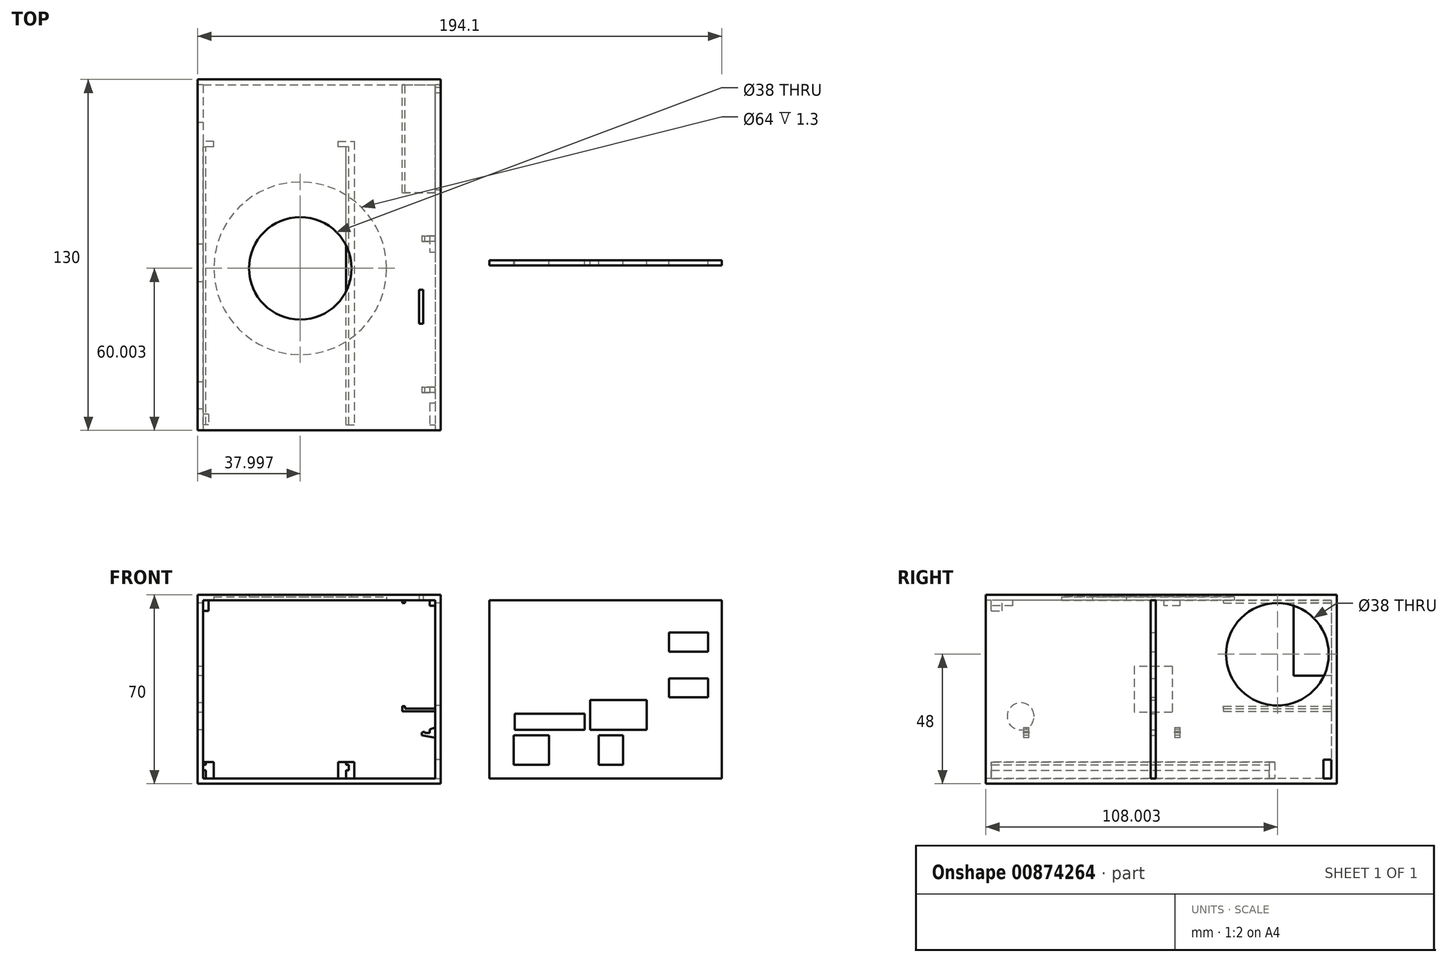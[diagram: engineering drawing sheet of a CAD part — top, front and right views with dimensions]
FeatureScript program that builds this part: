
annotation { "Feature Type Name" : "Feature", "Feature Type Description" : "" }
export const myFeature = defineFeature(function(context is Context, id is Id, definition is map)
    precondition{}
    {
        {
            var Q0;
            Q0=qCreatedBy(makeId("Top.planeOp"),FACE);
            var sketch = newSketch(context, id + "F0", { "sketchPlane" : qUnion([Q0])});
            skLineSegment(sketch, "E0.bottom", {"start": v(-34.75, 67) * mm, "end": v(55.25, 67) * mm});
            skLineSegment(sketch, "E0.top", {"start": v(-34.75, -63) * mm, "end": v(55.25, -63) * mm});
            skLineSegment(sketch, "E0.left", {"start": v(-34.75, 67) * mm, "end": v(-34.75, -63) * mm});
            skLineSegment(sketch, "E0.right", {"start": v(55.25, 67) * mm, "end": v(55.25, -63) * mm});
            skSolve(sketch);
        }
        {
            var Q0;
            Q0=makeQuery(id+"F0.imprint","IMPRINT",FACE,{"disambiguationData":[TD([[makeQuery(id+"F0.imprint","IMPRINT",EDGE,{"derivedFrom":sQuery(id+"F0.wireOp",EDGE,"E0.bottom")}),-1.0]])]});
            extrude(context, id + "F1", {"entities" : qUnion([Q0]), "depth" : 70 * mm, "offsetDistance" : 25 * mm});
        }
        {
            var Q0;
            Q0=makeQuery(id+"F1.opExtrude","SWEPT_FACE",FACE,{"disambiguationData":[OSD([sQuery(id+"F0.wireOp",EDGE,"E0.top")])]});
            var Q1;
            Q1=makeQuery(id+"F1.opExtrude","SWEPT_BODY",BODY,{"disambiguationData":[OSD([sQuery(id+"F0.wireOp",EDGE,"E0.bottom"),sQuery(id+"F0.wireOp",EDGE,"E0.top"),sQuery(id+"F0.wireOp",EDGE,"E0.left"),sQuery(id+"F0.wireOp",EDGE,"E0.right")])]});
            shell(context, id + "F2", {"entities" : qUnion([Q0]), "parts" : qUnion([Q1]), "thickness" : 2 * mm});
        }
        {
            var Q0;
            {var subQ0=sQuery(id+"F0.wireOp",EDGE,"E0.right");var subQ1=sQuery(id+"F0.wireOp",EDGE,"E0.left");var subQ2=sQuery(id+"F0.wireOp",EDGE,"E0.top");var subQ3=sQuery(id+"F0.wireOp",EDGE,"E0.bottom");Q0=makeQuery(id+"F2.opShell","OFFSET_FACE",FACE,{"disambiguationData":[OSD([subQ3,subQ2,subQ1,subQ0]),TDD([makeQuery(id+"F1.opExtrude","CAP_FACE",FACE,{"disambiguationData":[OSD([subQ3,subQ2,subQ1,subQ0])],"isStart":true})])]});}
            var sketch = newSketch(context, id + "F3", { "sketchPlane" : qUnion([Q0])});
            skLineSegment(sketch, "E1", {"start": v(-28.75, 42) * mm, "end": v(-28.75, 44) * mm});
            skLineSegment(sketch, "E2", {"start": v(17.25, 42) * mm, "end": v(17.25, 44) * mm});
            skLineSegment(sketch, "E3", {"start": v(17.25, 44) * mm, "end": v(23.25, 44) * mm});
            skLineSegment(sketch, "E4", {"start": v(23.25, 44) * mm, "end": v(23.25, 42) * mm});
            skLineSegment(sketch, "E5", {"start": v(-28.75, 44) * mm, "end": v(-32.75, 44) * mm});
            skLineSegment(sketch, "E6", {"start": v(-32.75, 44) * mm, "end": v(-32.75, 42) * mm});
            skLineSegment(sketch, "E7", {"start": v(23.25, 42) * mm, "end": v(17.25, 42) * mm});
            skLineSegment(sketch, "E8", {"start": v(-28.75, 42) * mm, "end": v(-32.75, 42) * mm});
            skSolve(sketch);
        }
        {
            var Q0;
            Q0=makeQuery(id+"F3.imprint","IMPRINT",FACE,{"disambiguationData":[TD([[makeQuery(id+"F3.imprint","IMPRINT",EDGE,{"derivedFrom":sQuery(id+"F3.wireOp",EDGE,"E1")}),1.0]])]});
            var Q1;
            Q1=makeQuery(id+"F3.imprint","IMPRINT",FACE,{"disambiguationData":[TD([[makeQuery(id+"F3.imprint","IMPRINT",EDGE,{"derivedFrom":sQuery(id+"F3.wireOp",EDGE,"E2")}),-1.0]])]});
            extrude(context, id + "F4", {"entities" : qUnion([Q0, Q1]), "operationType" : NewBodyOperationType.ADD, "depth" : 6 * mm, "offsetDistance" : 25 * mm});
        }
        {
            var Q0;
            Q0=makeQuery(id+"F4.opExtrude","SWEPT_FACE",FACE,{"disambiguationData":[OSD([sQuery(id+"F3.wireOp",EDGE,"E8")])]});
            var sketch = newSketch(context, id + "F5", { "sketchPlane" : qUnion([Q0])});
            skLineSegment(sketch, "E9", {"start": v(-32.75, 2) * mm, "end": v(-31.75, 2) * mm});
            skLineSegment(sketch, "E10", {"start": v(-31.75, 2) * mm, "end": v(-31.75, 5) * mm});
            skLineSegment(sketch, "E11", {"start": v(-31.75, 5) * mm, "end": v(-32.75, 5) * mm});
            skLineSegment(sketch, "E12", {"start": v(-32.75, 5) * mm, "end": v(-32.75, 2) * mm});
            skLineSegment(sketch, "E13", {"start": v(21.25, 7) * mm, "end": v(21.25, 5) * mm});
            skLineSegment(sketch, "E14", {"start": v(21.25, 5) * mm, "end": v(20.25, 5) * mm});
            skLineSegment(sketch, "E15", {"start": v(20.25, 5) * mm, "end": v(20.25, 2) * mm});
            skLineSegment(sketch, "E16", {"start": v(20.25, 2) * mm, "end": v(23.25, 2) * mm});
            skLineSegment(sketch, "E17", {"start": v(23.25, 2) * mm, "end": v(23.25, 8) * mm});
            skLineSegment(sketch, "E18", {"start": v(23.25, 8) * mm, "end": v(20.25, 8) * mm});
            skLineSegment(sketch, "E19", {"start": v(20.25, 8) * mm, "end": v(20.25, 7) * mm});
            skLineSegment(sketch, "E20", {"start": v(20.25, 7) * mm, "end": v(21.25, 7) * mm});
            skLineSegment(sketch, "E21.bottom", {"start": v(-32.75, 8) * mm, "end": v(-31.75, 8) * mm});
            skLineSegment(sketch, "E21.top", {"start": v(-32.75, 7) * mm, "end": v(-31.75, 7) * mm});
            skLineSegment(sketch, "E21.left", {"start": v(-32.75, 8) * mm, "end": v(-32.75, 7) * mm});
            skLineSegment(sketch, "E21.right", {"start": v(-31.75, 8) * mm, "end": v(-31.75, 7) * mm});
            skSolve(sketch);
        }
        {
            var Q0;
            Q0=makeQuery(id+"F5.imprint","IMPRINT",FACE,{"disambiguationData":[TD([[makeQuery(id+"F5.imprint","IMPRINT",EDGE,{"derivedFrom":sQuery(id+"F5.wireOp",EDGE,"E13")}),1.0]])]});
            var Q1;
            Q1=makeQuery(id+"F5.imprint","IMPRINT",FACE,{"disambiguationData":[TD([[makeQuery(id+"F5.imprint","IMPRINT",EDGE,{"derivedFrom":sQuery(id+"F5.wireOp",EDGE,"7ee66804-56aa-43c3-9890-e0b70faa4ac7")}),1.0]])]});
            var Q2;
            Q2=makeQuery(id+"F5.imprint","IMPRINT",FACE,{"disambiguationData":[TD([[makeQuery(id+"F5.imprint","IMPRINT",EDGE,{"derivedFrom":sQuery(id+"F5.wireOp",EDGE,"E9")}),-1.0]])]});
            var Q3;
            Q3=makeQuery(id+"F5.imprint","IMPRINT",FACE,{"disambiguationData":[TD([[makeQuery(id+"F5.imprint","IMPRINT",EDGE,{"derivedFrom":sQuery(id+"F5.wireOp",EDGE,"E21.bottom")}),1.0]])]});
            extrude(context, id + "F6", {"entities" : qUnion([Q0, Q1, Q2, Q3]), "operationType" : NewBodyOperationType.ADD, "depth" : 103 * mm, "offsetDistance" : 25 * mm});
        }
        {
            var Q0;
            Q0=makeQuery(id+"F2.opShell","OFFSET_FACE",FACE,{"disambiguationData":[OSD([sQuery(id+"F0.wireOp",EDGE,"E0.right")])]});
            var sketch = newSketch(context, id + "F7", { "sketchPlane" : qUnion([Q0])});
            skLineSegment(sketch, "E22", {"start": v(-9, 17.1) * mm, "end": v(-7, 17.1) * mm});
            skLineSegment(sketch, "E23", {"start": v(-7, 20.9) * mm, "end": v(-9, 20.9) * mm});
            skLineSegment(sketch, "E24", {"start": v(-9, 17.1) * mm, "end": v(-9, 20.9) * mm});
            skLineSegment(sketch, "E25", {"start": v(-7, 20.9) * mm, "end": v(-7, 17.1) * mm});
            skLineSegment(sketch, "E26", {"start": v(47, 17.1) * mm, "end": v(49, 17.1) * mm});
            skLineSegment(sketch, "E27", {"start": v(49, 20.9) * mm, "end": v(47, 20.9) * mm});
            skLineSegment(sketch, "E28", {"start": v(47, 17.1) * mm, "end": v(47, 20.9) * mm});
            skLineSegment(sketch, "E29", {"start": v(49, 20.9) * mm, "end": v(49, 17.1) * mm});
            skLineSegment(sketch, "E30", {"start": v(63, 68) * mm, "end": v(-7, 68) * mm});
            skLineSegment(sketch, "E31", {"start": v(-7, 68) * mm, "end": v(-7, 19) * mm});
            skSolve(sketch);
        }
        {
            var Q0;
            Q0=makeQuery(id+"F7.imprint","IMPRINT",FACE,{"disambiguationData":[TD([[makeQuery(id+"F7.imprint","IMPRINT",EDGE,{"derivedFrom":sQuery(id+"F7.wireOp",EDGE,"19951f1d-0f5a-4bec-891b-cc03b51abff4")}),-1.0]])]});
            var Q1;
            {var subQ0=sQuery(id+"F7.wireOp",EDGE,"E22");Q1=makeQuery(id+"F7.imprint","IMPRINT",FACE,{"disambiguationData":[TD([[makeQuery(id+"F7.imprint","IMPRINT",EDGE,{"derivedFrom":subQ0}),1.0]])]});}
            var Q2;
            {var subQ0=sQuery(id+"F7.wireOp",EDGE,"E23");Q2=makeQuery(id+"F7.imprint","IMPRINT",FACE,{"disambiguationData":[TD([[makeQuery(id+"F7.imprint","IMPRINT",EDGE,{"derivedFrom":subQ0}),1.0]])]});}
            var Q3;
            {var subQ0=sQuery(id+"F7.wireOp",EDGE,"E26");Q3=makeQuery(id+"F7.imprint","IMPRINT",FACE,{"disambiguationData":[TD([[makeQuery(id+"F7.imprint","IMPRINT",EDGE,{"derivedFrom":subQ0}),1.0]])]});}
            var Q4;
            {var subQ0=sQuery(id+"F7.wireOp",EDGE,"E27");Q4=makeQuery(id+"F7.imprint","IMPRINT",FACE,{"disambiguationData":[TD([[makeQuery(id+"F7.imprint","IMPRINT",EDGE,{"derivedFrom":subQ0}),1.0]])]});}
            extrude(context, id + "F8", {"entities" : qUnion([Q0, Q1, Q2, Q3, Q4]), "operationType" : NewBodyOperationType.ADD, "depth" : 5 * mm, "offsetDistance" : 25 * mm});
        }
        {
            var Q0;
            Q0=makeQuery(id+"F8.opExtrude","SWEPT_FACE",FACE,{"disambiguationData":[OSD([sQuery(id+"F7.wireOp",EDGE,"E29")])]});
            var sketch = newSketch(context, id + "F9", { "sketchPlane" : qUnion([Q0])});
            skLineSegment(sketch, "E32", {"start": v(53.25, 17.1) * mm, "end": v(48.25, 17.1) * mm});
            skLineSegment(sketch, "E33", {"start": v(48.25, 17.1) * mm, "end": v(48.25, 20.9) * mm});
            skLineSegment(sketch, "E34", {"start": v(48.25, 20.9) * mm, "end": v(53.25, 20.9) * mm});
            skLineSegment(sketch, "E35", {"start": v(53.25, 20.9) * mm, "end": v(51.25, 20.14) * mm});
            skLineSegment(sketch, "E36", {"start": v(51.25, 20.14) * mm, "end": v(51.25, 18.9) * mm});
            skLineSegment(sketch, "E37", {"start": v(51.25, 18.9) * mm, "end": v(49.25, 18.9) * mm});
            skLineSegment(sketch, "E38", {"start": v(49.25, 18.9) * mm, "end": v(49.25, 19.38) * mm});
            skLineSegment(sketch, "E39", {"start": v(48.25, 19) * mm, "end": v(48.25, 18) * mm});
            skLineSegment(sketch, "E40", {"start": v(48.25, 18) * mm, "end": v(53.25, 17.1) * mm});
            skLineSegment(sketch, "E41.trimOffspring", {"start": v(49.25, 19.38) * mm, "end": v(48.25, 19) * mm});
            skSolve(sketch);
        }
        {
            var Q0;
            {var subQ0=sQuery(id+"F9.wireOp",EDGE,"E34");Q0=makeQuery(id+"F9.imprint","IMPRINT",FACE,{"disambiguationData":[TD([[makeQuery(id+"F9.imprint","IMPRINT",EDGE,{"derivedFrom":subQ0}),-1.0]])]});}
            var Q1;
            {var subQ0=sQuery(id+"F9.wireOp",EDGE,"E32");Q1=makeQuery(id+"F9.imprint","IMPRINT",FACE,{"disambiguationData":[TD([[makeQuery(id+"F9.imprint","IMPRINT",EDGE,{"derivedFrom":subQ0}),1.0]])]});}
            extrude(context, id + "F10", {"entities" : qUnion([Q0, Q1]), "operationType" : NewBodyOperationType.REMOVE, "oppositeDirection" : true, "depth" : 70 * mm, "offsetDistance" : 25 * mm});
        }
        {
            var Q0;
            {var subQ0=sQuery(id+"F0.wireOp",EDGE,"E0.right");var subQ1=sQuery(id+"F0.wireOp",EDGE,"E0.left");var subQ2=sQuery(id+"F0.wireOp",EDGE,"E0.top");var subQ3=sQuery(id+"F0.wireOp",EDGE,"E0.bottom");Q0=makeQuery(id+"F2.opShell","OFFSET_FACE",FACE,{"disambiguationData":[OSD([subQ3,subQ2,subQ1,subQ0]),TDD([makeQuery(id+"F1.opExtrude","CAP_FACE",FACE,{"disambiguationData":[OSD([subQ3,subQ2,subQ1,subQ0])],"isStart":false})])]});}
            var sketch = newSketch(context, id + "F11", { "sketchPlane" : qUnion([Q0])});
            skLineSegment(sketch, "E42", {"start": v(49.25, -3.4) * mm, "end": v(49.25, 5) * mm});
            skLineSegment(sketch, "E43", {"start": v(49.25, 54) * mm, "end": v(49.25, 46) * mm});
            skLineSegment(sketch, "E44", {"start": v(49.25, 40) * mm, "end": v(49.25, 28) * mm});
            skLineSegment(sketch, "E45", {"start": v(49.25, 5) * mm, "end": v(49.25, -3.4) * mm});
            skLineSegment(sketch, "E46", {"start": v(49.25, -3.4) * mm, "end": v(42.75, -3.4) * mm});
            skLineSegment(sketch, "E47", {"start": v(42.75, -3.4) * mm, "end": v(42.75, 5) * mm});
            skLineSegment(sketch, "E48", {"start": v(42.75, 5) * mm, "end": v(49.25, 5) * mm});
            skLineSegment(sketch, "E49", {"start": v(48.75, 11) * mm, "end": v(48.75, 23.5) * mm});
            skLineSegment(sketch, "E50", {"start": v(48.75, 23.5) * mm, "end": v(47.25, 23.5) * mm});
            skLineSegment(sketch, "E51", {"start": v(47.25, 23.5) * mm, "end": v(47.25, 11) * mm});
            skLineSegment(sketch, "E52", {"start": v(47.25, 11) * mm, "end": v(48.75, 11) * mm});
            skLineSegment(sketch, "E53.trimOffspring", {"start": v(49.25, 28) * mm, "end": v(49.25, 40) * mm});
            skLineSegment(sketch, "E54.trimOffspring", {"start": v(49.25, 46) * mm, "end": v(49.25, 54) * mm});
            skLineSegment(sketch, "E55", {"start": v(49.25, 54) * mm, "end": v(46.25, 54) * mm});
            skLineSegment(sketch, "E56", {"start": v(46.25, 54) * mm, "end": v(46.25, 46) * mm});
            skLineSegment(sketch, "E57", {"start": v(46.25, 46) * mm, "end": v(49.25, 46) * mm});
            skLineSegment(sketch, "E58", {"start": v(47.25, 42) * mm, "end": v(42.75, 42) * mm});
            skLineSegment(sketch, "E59", {"start": v(42.75, 42) * mm, "end": v(42.75, 26) * mm});
            skLineSegment(sketch, "E60", {"start": v(42.75, 26) * mm, "end": v(47.25, 26) * mm});
            skLineSegment(sketch, "E61", {"start": v(49.25, 40) * mm, "end": v(47.25, 42) * mm});
            skLineSegment(sketch, "E62", {"start": v(49.25, 28) * mm, "end": v(47.25, 26) * mm});
            skCircle(sketch, "E63", {"center": v(3.25, 3) * mm, "radius": 32 * mm});
            skLineSegment(sketch, "E64", {"start": v(51.25, -9) * mm, "end": v(51.25, -3) * mm});
            skLineSegment(sketch, "E65", {"start": v(51.25, 61) * mm, "end": v(53.25, 61) * mm});
            skLineSegment(sketch, "E66", {"start": v(53.25, 61) * mm, "end": v(53.25, 53) * mm});
            skLineSegment(sketch, "E67", {"start": v(53.25, 53) * mm, "end": v(51.25, 53) * mm});
            skLineSegment(sketch, "E68", {"start": v(51.25, -9) * mm, "end": v(53.25, -9) * mm});
            skLineSegment(sketch, "E69", {"start": v(53.25, -9) * mm, "end": v(53.25, 61) * mm});
            skLineSegment(sketch, "E70", {"start": v(51.25, -3) * mm, "end": v(53.25, -3) * mm});
            skLineSegment(sketch, "E71.trimOffspring", {"start": v(51.25, 53) * mm, "end": v(51.25, 61) * mm});
            skCircle(sketch, "E72", {"center": v(3.25, 3) * mm, "radius": 19 * mm});
            skSolve(sketch);
        }
        {
            var Q0;
            Q0=makeQuery(id+"F11.imprint","IMPRINT",FACE,{"disambiguationData":[TD([[makeQuery(id+"F11.imprint","IMPRINT",EDGE,{"derivedFrom":sQuery(id+"F11.wireOp",EDGE,"E45")}),-1.0]])]});
            var Q1;
            Q1=makeQuery(id+"F11.imprint","IMPRINT",FACE,{"disambiguationData":[TD([[makeQuery(id+"F11.imprint","IMPRINT",EDGE,{"derivedFrom":sQuery(id+"F11.wireOp",EDGE,"E49")}),1.0]])]});
            var Q2;
            Q2=makeQuery(id+"F11.imprint","IMPRINT",FACE,{"disambiguationData":[TD([[makeQuery(id+"F11.imprint","IMPRINT",EDGE,{"derivedFrom":sQuery(id+"F11.wireOp",EDGE,"E53.trimOffspring")}),1.0]])]});
            var Q3;
            Q3=makeQuery(id+"F11.imprint","IMPRINT",FACE,{"disambiguationData":[TD([[makeQuery(id+"F11.imprint","IMPRINT",EDGE,{"derivedFrom":sQuery(id+"F11.wireOp",EDGE,"E54.trimOffspring")}),1.0]])]});
            var Q4;
            Q4=makeQuery(id+"F11.imprint","IMPRINT",FACE,{"disambiguationData":[TD([[makeQuery(id+"F11.imprint","IMPRINT",EDGE,{"derivedFrom":sQuery(id+"F11.wireOp",EDGE,"E72")}),1.0]])]});
            extrude(context, id + "F12", {"entities" : qUnion([Q0, Q1, Q2, Q3, Q4]), "operationType" : NewBodyOperationType.REMOVE, "oppositeDirection" : true, "depth" : 2 * mm, "offsetDistance" : 25 * mm});
        }
        {
            var Q0;
            Q0=makeQuery(id+"F11.imprint","IMPRINT",FACE,{"disambiguationData":[TD([[makeQuery(id+"F11.imprint","IMPRINT",EDGE,{"derivedFrom":sQuery(id+"F11.wireOp",EDGE,"E63")}),1.0]])]});
            extrude(context, id + "F13", {"entities" : qUnion([Q0]), "operationType" : NewBodyOperationType.REMOVE, "oppositeDirection" : true, "depth" : 1.3 * mm, "offsetDistance" : 25 * mm});
        }
        {
            var Q0;
            {var subQ0=sQuery(id+"F11.wireOp",EDGE,"E68");Q0=makeQuery(id+"F11.imprint","IMPRINT",FACE,{"disambiguationData":[TD([[makeQuery(id+"F11.imprint","IMPRINT",EDGE,{"derivedFrom":subQ0}),1.0]])]});}
            var Q1;
            {var subQ0=sQuery(id+"F11.wireOp",EDGE,"E65");Q1=makeQuery(id+"F11.imprint","IMPRINT",FACE,{"disambiguationData":[TD([[makeQuery(id+"F11.imprint","IMPRINT",EDGE,{"derivedFrom":subQ0}),-1.0]])]});}
            extrude(context, id + "F14", {"entities" : qUnion([Q0, Q1]), "operationType" : NewBodyOperationType.ADD, "depth" : 2 * mm, "offsetDistance" : 25 * mm});
        }
        {
            var Q0;
            Q0=makeQuery(id+"F2.opShell","OFFSET_FACE",FACE,{"disambiguationData":[OSD([sQuery(id+"F0.wireOp",EDGE,"E0.bottom")])]});
            var sketch = newSketch(context, id + "F15", { "sketchPlane" : qUnion([Q0])});
            skLineSegment(sketch, "E73", {"start": v(53.25, 68) * mm, "end": v(42.05, 68) * mm});
            skLineSegment(sketch, "E74", {"start": v(42.05, 68) * mm, "end": v(42.05, 67) * mm});
            skLineSegment(sketch, "E75", {"start": v(42.05, 67) * mm, "end": v(41.05, 67) * mm});
            skLineSegment(sketch, "E76", {"start": v(41.05, 67) * mm, "end": v(41.05, 68) * mm});
            skLineSegment(sketch, "E77", {"start": v(53.25, 68) * mm, "end": v(53.25, 27.8) * mm});
            skLineSegment(sketch, "E78", {"start": v(53.25, 27.8) * mm, "end": v(42.05, 27.8) * mm});
            skLineSegment(sketch, "E79", {"start": v(42.05, 27.8) * mm, "end": v(42.05, 28.8) * mm});
            skLineSegment(sketch, "E80", {"start": v(42.05, 28.8) * mm, "end": v(41.05, 28.8) * mm});
            skLineSegment(sketch, "E81", {"start": v(41.05, 28.8) * mm, "end": v(41.05, 26.8) * mm});
            skLineSegment(sketch, "E82", {"start": v(41.05, 26.8) * mm, "end": v(53.25, 26.8) * mm});
            skSolve(sketch);
        }
        {
            var Q0;
            {var subQ0=sQuery(id+"F15.wireOp",EDGE,"E78");Q0=makeQuery(id+"F15.imprint","IMPRINT",FACE,{"disambiguationData":[TD([[makeQuery(id+"F15.imprint","IMPRINT",EDGE,{"derivedFrom":subQ0}),1.0]])]});}
            var Q1;
            {var subQ0=sQuery(id+"F15.wireOp",EDGE,"E74");Q1=makeQuery(id+"F15.imprint","IMPRINT",FACE,{"disambiguationData":[TD([[makeQuery(id+"F15.imprint","IMPRINT",EDGE,{"derivedFrom":subQ0}),-1.0]])]});}
            extrude(context, id + "F16", {"entities" : qUnion([Q0, Q1]), "operationType" : NewBodyOperationType.ADD, "depth" : 40 * mm, "offsetDistance" : 25 * mm});
        }
        {
            var Q0;
            Q0=makeQuery(id+"F2.opShell","OFFSET_FACE",FACE,{"disambiguationData":[OSD([sQuery(id+"F0.wireOp",EDGE,"E0.right")])]});
            var sketch = newSketch(context, id + "F17", { "sketchPlane" : qUnion([Q0])});
            skCircle(sketch, "E83", {"center": v(-45, 48) * mm, "radius": 19 * mm});
            skSolve(sketch);
        }
        {
            var Q0;
            Q0=makeQuery(id+"F17.imprint","IMPRINT",FACE,{"disambiguationData":[TD([[makeQuery(id+"F17.imprint","IMPRINT",EDGE,{"derivedFrom":sQuery(id+"F17.wireOp",EDGE,"E83")}),1.0]])]});
            extrude(context, id + "F18", {"entities" : qUnion([Q0]), "operationType" : NewBodyOperationType.REMOVE, "oppositeDirection" : true, "depth" : 2 * mm, "offsetDistance" : 25 * mm});
        }
        {
            var Q0;
            Q0=qCreatedBy(makeId("Front.planeOp"),FACE);
            var sketch = newSketch(context, id + "F19", { "sketchPlane" : qUnion([Q0])});
            skLineSegment(sketch, "E84.left", {"start": v(159.35, 68) * mm, "end": v(159.35, 2) * mm});
            skLineSegment(sketch, "E85.MirrorCS", {"start": v(139.85, 39) * mm, "end": v(139.85, 32) * mm});
            skLineSegment(sketch, "E86.MirrorCS", {"start": v(110.65, 31) * mm, "end": v(110.65, 20) * mm});
            skLineSegment(sketch, "E87.MirrorCS", {"start": v(154.35, 32) * mm, "end": v(154.35, 39) * mm});
            skLineSegment(sketch, "E88.MirrorCS", {"start": v(108.65, 20) * mm, "end": v(108.65, 26) * mm});
            skLineSegment(sketch, "E89.MirrorCS", {"start": v(154.35, 49) * mm, "end": v(154.35, 56) * mm});
            skLineSegment(sketch, "E90.MirrorCS", {"start": v(82.65, 26) * mm, "end": v(82.65, 20) * mm});
            skLineSegment(sketch, "E91.MirrorCS", {"start": v(139.85, 56) * mm, "end": v(139.85, 49) * mm});
            skLineSegment(sketch, "E92.MirrorCS", {"start": v(139.85, 49) * mm, "end": v(154.35, 49) * mm});
            skLineSegment(sketch, "E93.MirrorCS", {"start": v(113.85, 18) * mm, "end": v(113.85, 7) * mm});
            skLineSegment(sketch, "E94.MirrorCS", {"start": v(113.85, 7) * mm, "end": v(122.85, 7) * mm});
            skLineSegment(sketch, "E95.MirrorCS", {"start": v(154.35, 39) * mm, "end": v(139.85, 39) * mm});
            skLineSegment(sketch, "E96.MirrorCS", {"start": v(122.85, 18) * mm, "end": v(113.85, 18) * mm});
            skLineSegment(sketch, "E97.MirrorCS", {"start": v(122.85, 18) * mm, "end": v(122.85, 7) * mm});
            skLineSegment(sketch, "E98.MirrorCS", {"start": v(82.35, 7) * mm, "end": v(95.35, 7) * mm});
            skLineSegment(sketch, "E99.MirrorCS", {"start": v(95.35, 18) * mm, "end": v(82.35, 18) * mm});
            skLineSegment(sketch, "E100.MirrorCS", {"start": v(131.65, 20) * mm, "end": v(131.65, 31) * mm});
            skLineSegment(sketch, "E101.MirrorCS", {"start": v(154.35, 56) * mm, "end": v(139.85, 56) * mm});
            skLineSegment(sketch, "E102.MirrorCS", {"start": v(95.35, 7) * mm, "end": v(95.35, 18) * mm});
            skLineSegment(sketch, "E103.MirrorCS", {"start": v(159.35, 68) * mm, "end": v(73.35, 68) * mm});
            skLineSegment(sketch, "E104.MirrorCS", {"start": v(108.65, 26) * mm, "end": v(82.65, 26) * mm});
            skLineSegment(sketch, "E105.MirrorCS", {"start": v(82.35, 18) * mm, "end": v(82.35, 7) * mm});
            skLineSegment(sketch, "E106.MirrorCS", {"start": v(139.85, 32) * mm, "end": v(154.35, 32) * mm});
            skLineSegment(sketch, "E107.MirrorCS", {"start": v(131.65, 31) * mm, "end": v(110.65, 31) * mm});
            skLineSegment(sketch, "E108.MirrorCS", {"start": v(131.65, 20) * mm, "end": v(110.65, 20) * mm});
            skLineSegment(sketch, "E109.MirrorCS", {"start": v(159.35, 2) * mm, "end": v(73.35, 2) * mm});
            skLineSegment(sketch, "E110.MirrorCS", {"start": v(73.35, 68) * mm, "end": v(73.35, 2) * mm});
            skLineSegment(sketch, "E111.MirrorCS", {"start": v(82.65, 20) * mm, "end": v(108.65, 20) * mm});
            skSolve(sketch);
        }
        {
            var Q0;
            Q0=makeQuery(id+"F19.imprint","IMPRINT",FACE,{"disambiguationData":[TD([[makeQuery(id+"F19.imprint","IMPRINT",EDGE,{"derivedFrom":sQuery(id+"F19.wireOp",EDGE,"E84.left")}),-1.0]])]});
            extrude(context, id + "F20", {"entities" : qUnion([Q0]), "depth" : 2 * mm, "offsetDistance" : 25 * mm});
        }
        {
            var Q0;
            Q0=makeQuery(id+"F2.opShell","OFFSET_FACE",FACE,{"disambiguationData":[OSD([sQuery(id+"F0.wireOp",EDGE,"E0.right")])]});
            var sketch = newSketch(context, id + "F21", { "sketchPlane" : qUnion([Q0])});
            skPoint(sketch, "E112.oppositeSnap0", {"position": v(-65, 9) * mm});
            skLineSegment(sketch, "E112.bottom", {"start": v(-65, 2) * mm, "end": v(-62, 2) * mm});
            skLineSegment(sketch, "E112.top", {"start": v(-65, 9) * mm, "end": v(-62, 9) * mm});
            skLineSegment(sketch, "E112.left", {"start": v(-65, 2) * mm, "end": v(-65, 9) * mm});
            skLineSegment(sketch, "E112.right", {"start": v(-62, 2) * mm, "end": v(-62, 9) * mm});
            skSolve(sketch);
        }
        {
            var Q0;
            Q0=makeQuery(id+"F21.imprint","IMPRINT",FACE,{"disambiguationData":[TD([[makeQuery(id+"F21.imprint","IMPRINT",EDGE,{"derivedFrom":sQuery(id+"F21.wireOp",EDGE,"E112.bottom")}),1.0]])]});
            extrude(context, id + "F22", {"entities" : qUnion([Q0]), "operationType" : NewBodyOperationType.REMOVE, "oppositeDirection" : true, "depth" : 2 * mm, "offsetDistance" : 25 * mm});
        }
        {
            var Q0;
            Q0=makeQuery(id+"F1.opExtrude","SWEPT_FACE",FACE,{"disambiguationData":[OSD([sQuery(id+"F0.wireOp",EDGE,"E0.left")])]});
            var sketch = newSketch(context, id + "F23", { "sketchPlane" : qUnion([Q0])});
            skLineSegment(sketch, "E113.bottom", {"start": v(-6, 43.5) * mm, "end": v(8, 43.5) * mm});
            skLineSegment(sketch, "E113.top", {"start": v(-6, 26.5) * mm, "end": v(8, 26.5) * mm});
            skLineSegment(sketch, "E113.left", {"start": v(-6, 43.5) * mm, "end": v(-6, 26.5) * mm});
            skLineSegment(sketch, "E113.right", {"start": v(8, 43.5) * mm, "end": v(8, 26.5) * mm});
            skLineSegment(sketch, "E114.bottom", {"start": v(-65, 67) * mm, "end": v(-51, 67) * mm});
            skLineSegment(sketch, "E114.top", {"start": v(-65, 40) * mm, "end": v(-51, 40) * mm});
            skLineSegment(sketch, "E114.left", {"start": v(-65, 67) * mm, "end": v(-65, 40) * mm});
            skLineSegment(sketch, "E114.right", {"start": v(-51, 67) * mm, "end": v(-51, 40) * mm});
            skCircle(sketch, "E115", {"center": v(50.1, 25) * mm, "radius": 5 * mm});
            skLineSegment(sketch, "E116.bottom", {"start": v(57, 68) * mm, "end": v(61, 68) * mm});
            skLineSegment(sketch, "E116.top", {"start": v(57, 64) * mm, "end": v(61, 64) * mm});
            skLineSegment(sketch, "E116.left", {"start": v(57, 68) * mm, "end": v(57, 64) * mm});
            skLineSegment(sketch, "E116.right", {"start": v(61, 68) * mm, "end": v(61, 64) * mm});
            skSolve(sketch);
        }
        {
            var Q0;
            Q0=makeQuery(id+"F23.imprint","IMPRINT",FACE,{"disambiguationData":[TD([[makeQuery(id+"F23.imprint","IMPRINT",EDGE,{"derivedFrom":sQuery(id+"F23.wireOp",EDGE,"E114.bottom")}),-1.0]])]});
            var Q1;
            Q1=makeQuery(id+"F23.imprint","IMPRINT",FACE,{"disambiguationData":[TD([[makeQuery(id+"F23.imprint","IMPRINT",EDGE,{"derivedFrom":sQuery(id+"F23.wireOp",EDGE,"E113.bottom")}),-1.0]])]});
            var Q2;
            Q2=makeQuery(id+"F23.imprint","IMPRINT",FACE,{"disambiguationData":[TD([[makeQuery(id+"F23.imprint","IMPRINT",EDGE,{"derivedFrom":sQuery(id+"F23.wireOp",EDGE,"E115")}),1.0]])]});
            extrude(context, id + "F24", {"entities" : qUnion([Q0, Q1, Q2]), "operationType" : NewBodyOperationType.REMOVE, "oppositeDirection" : true, "depth" : 2 * mm, "offsetDistance" : 25 * mm});
        }
        {
            var Q0;
            Q0=makeQuery(id+"F23.imprint","IMPRINT",FACE,{"disambiguationData":[TD([[makeQuery(id+"F23.imprint","IMPRINT",EDGE,{"derivedFrom":sQuery(id+"F23.wireOp",EDGE,"E116.bottom")}),-1.0]])]});
            extrude(context, id + "F25", {"entities" : qUnion([Q0]), "operationType" : NewBodyOperationType.ADD, "oppositeDirection" : true, "depth" : 4 * mm, "offsetDistance" : 25 * mm});
        }
    });
